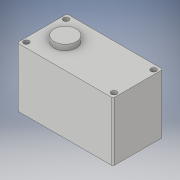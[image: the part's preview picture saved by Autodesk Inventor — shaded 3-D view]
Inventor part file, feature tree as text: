
AUTODESK INVENTOR PART (.ipt)
format: ipt  version: 2019 (Build 230136000, 136)  size: 121,344 bytes
history: native  units: in
note: dims shown in document units (in); Inventor stores cm internally (conversion verified against a paired STEP export)
features: extrude x2, sketch x1, hole x1, chamfer x1
ambient origin geometry x8: Origin, YZ Plane, XZ Plane, XY Plane, X Axis, Y Axis, Z Axis, Center Point
bodies: Solid1 (feature_tree)
feature tree (5):
  sketch  "Sketch1"  dims[d0=0.7165in d1=1.5827in d2=1.7331in d3=0.9024in d4=1.3134in d5=0.4in d6=1.063in d7=0.0in d8=0.0984in d9=0.5in d10=0.375in d11=0.25in d12=0.5635in d13=0.75in d14=0.8108in d15=0.0197in d16=0.125in d17=45.0deg d18=1.2646in d19=0.0in]
  extrude  "Extrusion1"  Depth=1.2646in
  hole  "Hole1"  [1 undecoded]
  chamfer  "Chamfer1"  Distance=0.9024in
  extrude  "Extrusion2"  Depth=1.2646in
note: 1 required parameter value undecoded (feature->parameter linkage not recoverable at this tier; creation-order binding heuristic only, values carry confidence <= 0.55)
